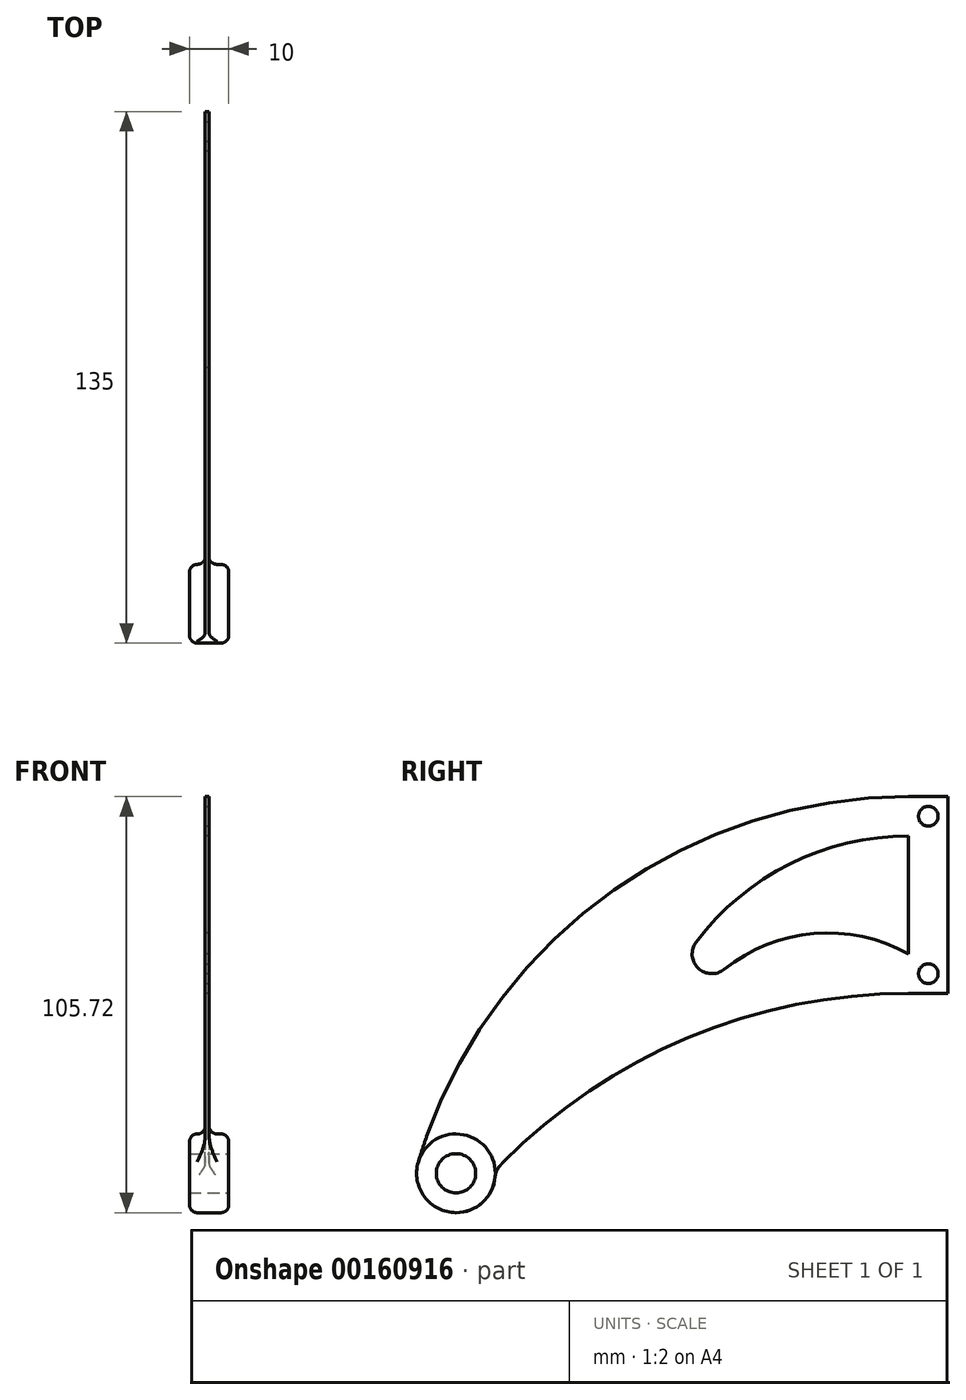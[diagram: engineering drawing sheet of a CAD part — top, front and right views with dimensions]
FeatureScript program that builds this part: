
annotation { "Feature Type Name" : "Feature", "Feature Type Description" : "" }
export const myFeature = defineFeature(function(context is Context, id is Id, definition is map)
    precondition{}
    {
        {
            var Q0;
            Q0=qCreatedBy(makeId("Right.planeOp"),FACE);
            var sketch = newSketch(context, id + "F0", { "sketchPlane" : qUnion([Q0])});
            skLineSegment(sketch, "E0.bottom", {"start": v(5, -25) * mm, "end": v(-5, -25) * mm});
            skLineSegment(sketch, "E0.top", {"start": v(5, 25) * mm, "end": v(-5, 25) * mm});
            skLineSegment(sketch, "E0.left", {"start": v(5, -25) * mm, "end": v(5, 25) * mm});
            skPoint(sketch, "E0.middle", {"position": v(0, 0) * mm});
            skPoint(sketch, "E1.endSnap0", {"position": v(0, -25) * mm});
            skArc(sketch, "E2", {"start": v(-129.58, -67.87) * mm, "mid": v(-121.9, -80.54) * mm, "end": v(-110.04, -71.63) * mm});
            skArc(sketch, "E3", {"start": v(-5, 25) * mm, "mid": v(-82.7, -0.77) * mm, "end": v(-129.58, -67.87) * mm});
            skArc(sketch, "E4", {"start": v(-5, -25) * mm, "mid": v(-61.21, -36.34) * mm, "end": v(-108.64, -68.59) * mm});
            skPoint(sketch, "E1.start.orphan", {"position": v(0, -25) * mm});
            skPoint(sketch, "E5.orphan", {"position": v(0, -75) * mm});
            skLineSegment(sketch, "E6", {"start": v(-5, 15) * mm, "end": v(-5, -15) * mm});
            skArc(sketch, "E7", {"start": v(-59, -12) * mm, "mid": v(-58.48, -18.6) * mm, "end": v(-51.88, -18.9) * mm});
            skArc(sketch, "E8", {"start": v(-5, 15) * mm, "mid": v(-35.19, 7.87) * mm, "end": v(-59, -12) * mm});
            skArc(sketch, "E9", {"start": v(-5, -15) * mm, "mid": v(-29.03, -9.81) * mm, "end": v(-51.88, -18.9) * mm});
            skPoint(sketch, "E10.visualSharp", {"position": v(-110.02, -70.03) * mm});
            skArc(sketch, "E10.filletArc", {"start": v(-108.64, -68.59) * mm, "mid": v(-109.6, -69.99) * mm, "end": v(-110.04, -71.63) * mm});
            skSolve(sketch);
        }
        {
            var Q0;
            Q0 = qSketchRegion(id + "F0", true);
            extrude(context, id + "F1", {"entities" : qUnion([Q0]), "depth" : 0.5 * mm, "hasSecondDirection" : true, "secondDirectionOppositeDirection" : true, "secondDirectionDepth" : 0.5 * mm});
        }
        {
            var Q0;
            Q0=makeQuery(id+"F1.opExtrude","CAP_FACE",FACE,{"disambiguationData":[OSD([sQuery(id+"F0.wireOp",EDGE,"E0.bottom"),sQuery(id+"F0.wireOp",EDGE,"E0.top"),sQuery(id+"F0.wireOp",EDGE,"E0.left"),sQuery(id+"F0.wireOp",EDGE,"E2"),sQuery(id+"F0.wireOp",EDGE,"E3"),sQuery(id+"F0.wireOp",EDGE,"E4"),sQuery(id+"F0.wireOp",EDGE,"E6"),sQuery(id+"F0.wireOp",EDGE,"E7"),sQuery(id+"F0.wireOp",EDGE,"E8"),sQuery(id+"F0.wireOp",EDGE,"E9")])],"isStart":false});
            var sketch = newSketch(context, id + "F2", { "sketchPlane" : qUnion([Q0])});
            skCircle(sketch, "E11", {"center": v(-120, -70.72) * mm, "radius": 10 * mm});
            skSolve(sketch);
        }
        {
            var Q0;
            Q0 = qSketchRegion(id + "F2", true);
            extrude(context, id + "F3", {"entities" : qUnion([Q0]), "operationType" : NewBodyOperationType.ADD, "depth" : 5 * mm, "hasSecondDirection" : true, "secondDirectionOppositeDirection" : true, "secondDirectionDepth" : 5 * mm});
        }
        {
            var Q0;
            Q0=makeQuery(id+"F3.boolean.opBoolean","MERGE",FACE,{"derivedFrom":[makeQuery(id+"F1.opExtrude","SWEPT_FACE",FACE,{"disambiguationData":[OSD([sQuery(id+"F0.wireOp",EDGE,"E2")])]}),makeQuery(id+"F3.opExtrude","SWEPT_FACE",FACE,{"disambiguationData":[OSD([sQuery(id+"F2.wireOp",EDGE,"E11")])]})]});
            fillet(context, id + "F4", {"entities" : qUnion([Q0]), "radius" : 2 * mm, "tangentPropagation" : true, "allowEdgeOverflow" : false});
        }
        {
            var Q0;
            Q0=makeQuery(id+"F3.opExtrude","CAP_FACE",FACE,{"disambiguationData":[OSD([sQuery(id+"F2.wireOp",EDGE,"E11")])],"isStart":false});
            var sketch = newSketch(context, id + "F5", { "sketchPlane" : qUnion([Q0])});
            skCircle(sketch, "E12", {"center": v(-120, -70.72) * mm, "radius": 5 * mm});
            skSolve(sketch);
        }
        {
            var Q0;
            Q0 = qSketchRegion(id + "F5", true);
            extrude(context, id + "F6", {"entities" : qUnion([Q0]), "operationType" : NewBodyOperationType.REMOVE, "oppositeDirection" : true, "depth" : 10 * mm});
        }
        {
            var Q0;
            Q0=makeQuery(id+"F1.opExtrude","CAP_FACE",FACE,{"disambiguationData":[OSD([sQuery(id+"F0.wireOp",EDGE,"E0.bottom"),sQuery(id+"F0.wireOp",EDGE,"E0.top"),sQuery(id+"F0.wireOp",EDGE,"E0.left"),sQuery(id+"F0.wireOp",EDGE,"E2"),sQuery(id+"F0.wireOp",EDGE,"E3"),sQuery(id+"F0.wireOp",EDGE,"E4"),sQuery(id+"F0.wireOp",EDGE,"E6"),sQuery(id+"F0.wireOp",EDGE,"E7"),sQuery(id+"F0.wireOp",EDGE,"E8"),sQuery(id+"F0.wireOp",EDGE,"E9")])],"isStart":false});
            var sketch = newSketch(context, id + "F7", { "sketchPlane" : qUnion([Q0])});
            skCircle(sketch, "E13", {"center": v(0, 20) * mm, "radius": 2.5 * mm});
            skCircle(sketch, "E14.MirrorC", {"center": v(0, -20) * mm, "radius": 2.5 * mm});
            skSolve(sketch);
        }
        {
            var Q0;
            Q0 = qSketchRegion(id + "F7", true);
            extrude(context, id + "F8", {"entities" : qUnion([Q0]), "operationType" : NewBodyOperationType.REMOVE, "oppositeDirection" : true, "depth" : 2 * mm});
        }
    });
